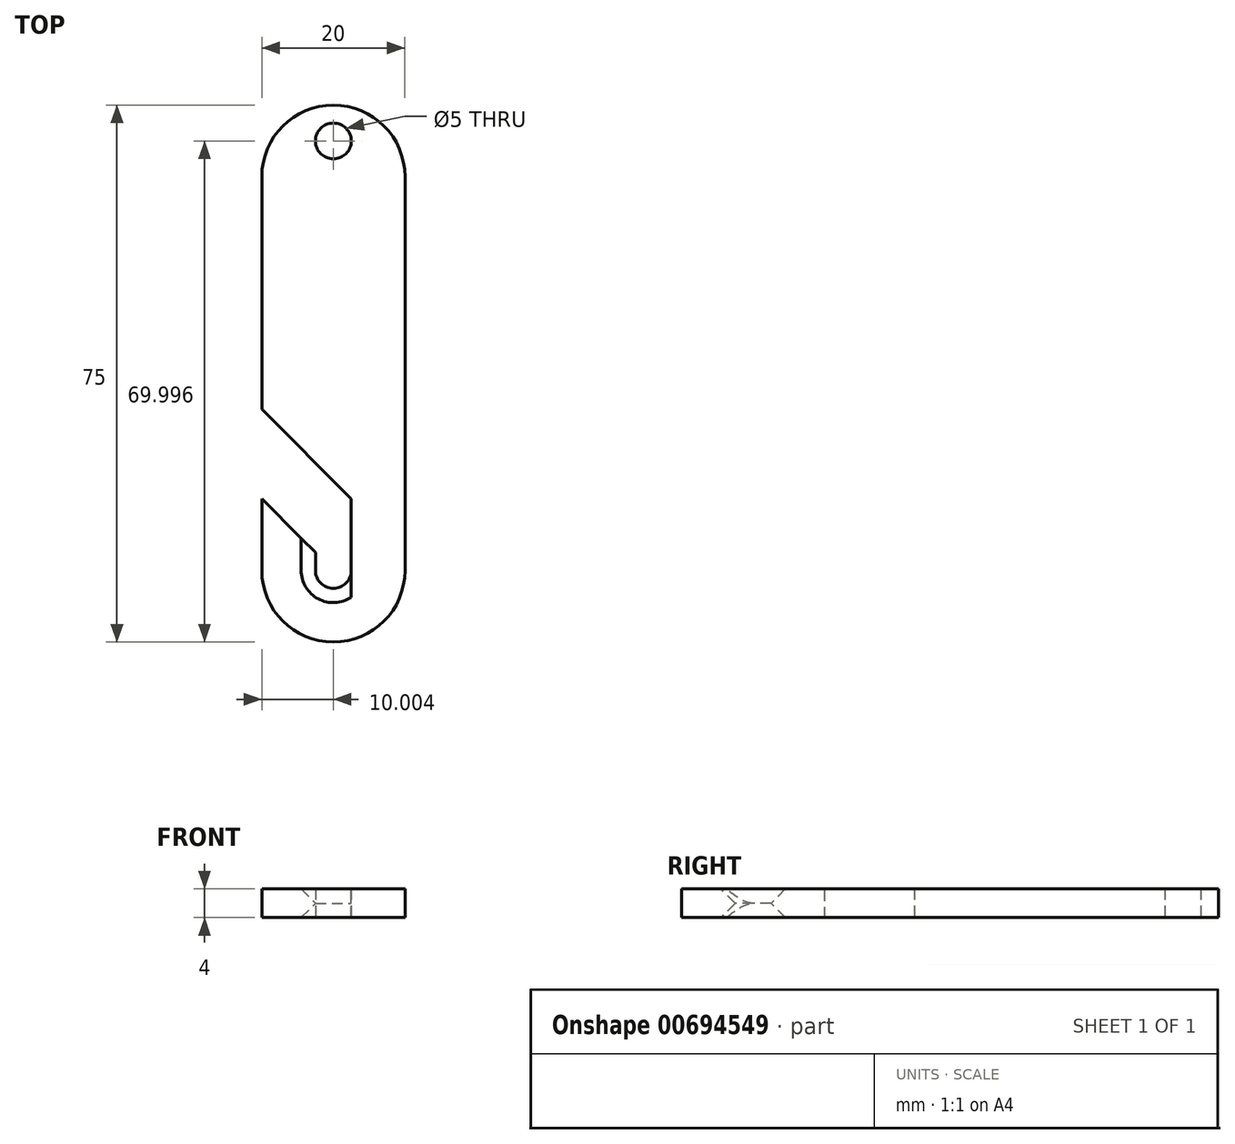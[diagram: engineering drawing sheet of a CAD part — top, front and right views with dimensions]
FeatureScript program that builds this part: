
annotation { "Feature Type Name" : "Feature", "Feature Type Description" : "" }
export const myFeature = defineFeature(function(context is Context, id is Id, definition is map)
    precondition{}
    {
        {
            var Q0;
            Q0=qCreatedBy(makeId("Top.planeOp"),FACE);
            var sketch = newSketch(context, id + "F0", { "sketchPlane" : qUnion([Q0])});
            skLineSegment(sketch, "E0.bottom", {"start": v(-26.12, 38.63) * mm, "end": v(-6.12, 38.63) * mm, "construction": true});
            skLineSegment(sketch, "E0.top", {"start": v(-26.12, -16.37) * mm, "end": v(-6.12, -16.37) * mm, "construction": true});
            skLineSegment(sketch, "E0.left", {"start": v(-26.12, 38.63) * mm, "end": v(-26.12, 6.13) * mm});
            skLineSegment(sketch, "E0.right", {"start": v(-6.12, 38.63) * mm, "end": v(-6.12, -16.37) * mm});
            skCircle(sketch, "E1", {"center": v(-16.12, 38.63) * mm, "radius": 10 * mm});
            skLineSegment(sketch, "E2", {"start": v(-16.12, 52.84) * mm, "end": v(-16.12, -33.2) * mm, "construction": true});
            skCircle(sketch, "E3", {"center": v(-16.12, 43.63) * mm, "radius": 2.5 * mm});
            skArc(sketch, "E4", {"start": v(-18.62, -16.37) * mm, "mid": v(-16.12, -18.87) * mm, "end": v(-13.62, -16.37) * mm});
            skLineSegment(sketch, "E5", {"start": v(-16.12, -6.37) * mm, "end": v(-40.56, -6.37) * mm, "construction": true});
            skLineSegment(sketch, "E6", {"start": v(-26.12, -6.37) * mm, "end": v(-18.62, -13.87) * mm});
            skLineSegment(sketch, "E7", {"start": v(-26.12, 6.13) * mm, "end": v(-16.12, -3.87) * mm});
            skLineSegment(sketch, "E8", {"start": v(-13.62, -16.37) * mm, "end": v(-13.62, -12.04) * mm});
            skLineSegment(sketch, "E9", {"start": v(-16.12, -3.87) * mm, "end": v(-13.62, -6.37) * mm});
            skArc(sketch, "E10", {"start": v(-26.12, -16.37) * mm, "mid": v(-16.12, -26.37) * mm, "end": v(-6.12, -16.37) * mm});
            skLineSegment(sketch, "E11", {"start": v(-18.62, -16.37) * mm, "end": v(-18.62, -13.87) * mm});
            skLineSegment(sketch, "E12.trimOffspring", {"start": v(-26.12, -6.37) * mm, "end": v(-26.12, -16.37) * mm});
            skArc(sketch, "E13", {"start": v(-21.12, -16.37) * mm, "mid": v(-18.62, -20.7) * mm, "end": v(-13.62, -20.7) * mm});
            skLineSegment(sketch, "E14", {"start": v(-21.12, -16.37) * mm, "end": v(-21.12, -11.37) * mm});
            skLineSegment(sketch, "E15", {"start": v(-13.62, -16.37) * mm, "end": v(-13.62, -20.7) * mm});
            skArc(sketch, "E16", {"start": v(-13.62, -12.04) * mm, "mid": v(-16.77, -11.42) * mm, "end": v(-19.65, -12.84) * mm, "construction": true});
            skLineSegment(sketch, "E17", {"start": v(-13.62, -12.04) * mm, "end": v(-13.62, -6.37) * mm});
            skSolve(sketch);
        }
        {
            var Q0;
            Q0 = qSketchRegion(id + "F0", true);
            extrude(context, id + "F1", {"entities" : qUnion([Q0]), "depth" : 4 * mm, "offsetDistance" : 25 * mm});
        }
        {
            var Q0;
            Q0=makeQuery(id+"F1.opExtrude","CAP_EDGE",EDGE,{"disambiguationData":[OSD([sQuery(id+"F0.wireOp",EDGE,"E4")])],"isStart":false});
            var Q1;
            Q1=makeQuery(id+"F1.opExtrude","CAP_EDGE",EDGE,{"disambiguationData":[OSD([sQuery(id+"F0.wireOp",EDGE,"E11")])],"isStart":false});
            var Q2;
            Q2=makeQuery(id+"F1.opExtrude","CAP_EDGE",EDGE,{"disambiguationData":[OSD([sQuery(id+"F0.wireOp",EDGE,"E4")])],"isStart":true});
            chamfer(context, id + "F2", {"entities" : qUnion([Q0, Q1, Q2]), "width" : 2 * mm, "tangentPropagation" : true});
        }
        {
            var Q0;
            Q0=makeQuery(id+"F1.opExtrude","CAP_FACE",FACE,{"disambiguationData":[OSD([sQuery(id+"F0.wireOp",EDGE,"E0.left"),sQuery(id+"F0.wireOp",EDGE,"E0.right"),sQuery(id+"F0.wireOp",EDGE,"E1"),sQuery(id+"F0.wireOp",EDGE,"E3"),sQuery(id+"F0.wireOp",EDGE,"E4"),sQuery(id+"F0.wireOp",EDGE,"E6"),sQuery(id+"F0.wireOp",EDGE,"E7"),sQuery(id+"F0.wireOp",EDGE,"E8"),sQuery(id+"F0.wireOp",EDGE,"E9"),sQuery(id+"F0.wireOp",EDGE,"E10"),sQuery(id+"F0.wireOp",EDGE,"E11"),sQuery(id+"F0.wireOp",EDGE,"E12.trimOffspring"),sQuery(id+"F0.wireOp",EDGE,"E17")])],"isStart":false});
            var sketch = newSketch(context, id + "F3", { "sketchPlane" : qUnion([Q0])});
            skPoint(sketch, "E18.0", {"position": v(-13.62, -6.37) * mm});
            skLineSegment(sketch, "E19.bottom", {"start": v(-13.62, -6.37) * mm, "end": v(-10.39, -6.37) * mm});
            skLineSegment(sketch, "E19.top", {"start": v(-13.62, -21.46) * mm, "end": v(-10.39, -21.46) * mm});
            skLineSegment(sketch, "E19.left", {"start": v(-13.62, -6.37) * mm, "end": v(-13.62, -21.46) * mm});
            skLineSegment(sketch, "E19.right", {"start": v(-10.39, -6.37) * mm, "end": v(-10.39, -21.46) * mm});
            skSolve(sketch);
        }
        {
            var Q0;
            Q0 = qSketchRegion(id + "F3", true);
            extrude(context, id + "F4", {"entities" : qUnion([Q0]), "operationType" : NewBodyOperationType.ADD, "oppositeDirection" : true, "depth" : 4 * mm, "offsetDistance" : 25 * mm});
        }
    });
